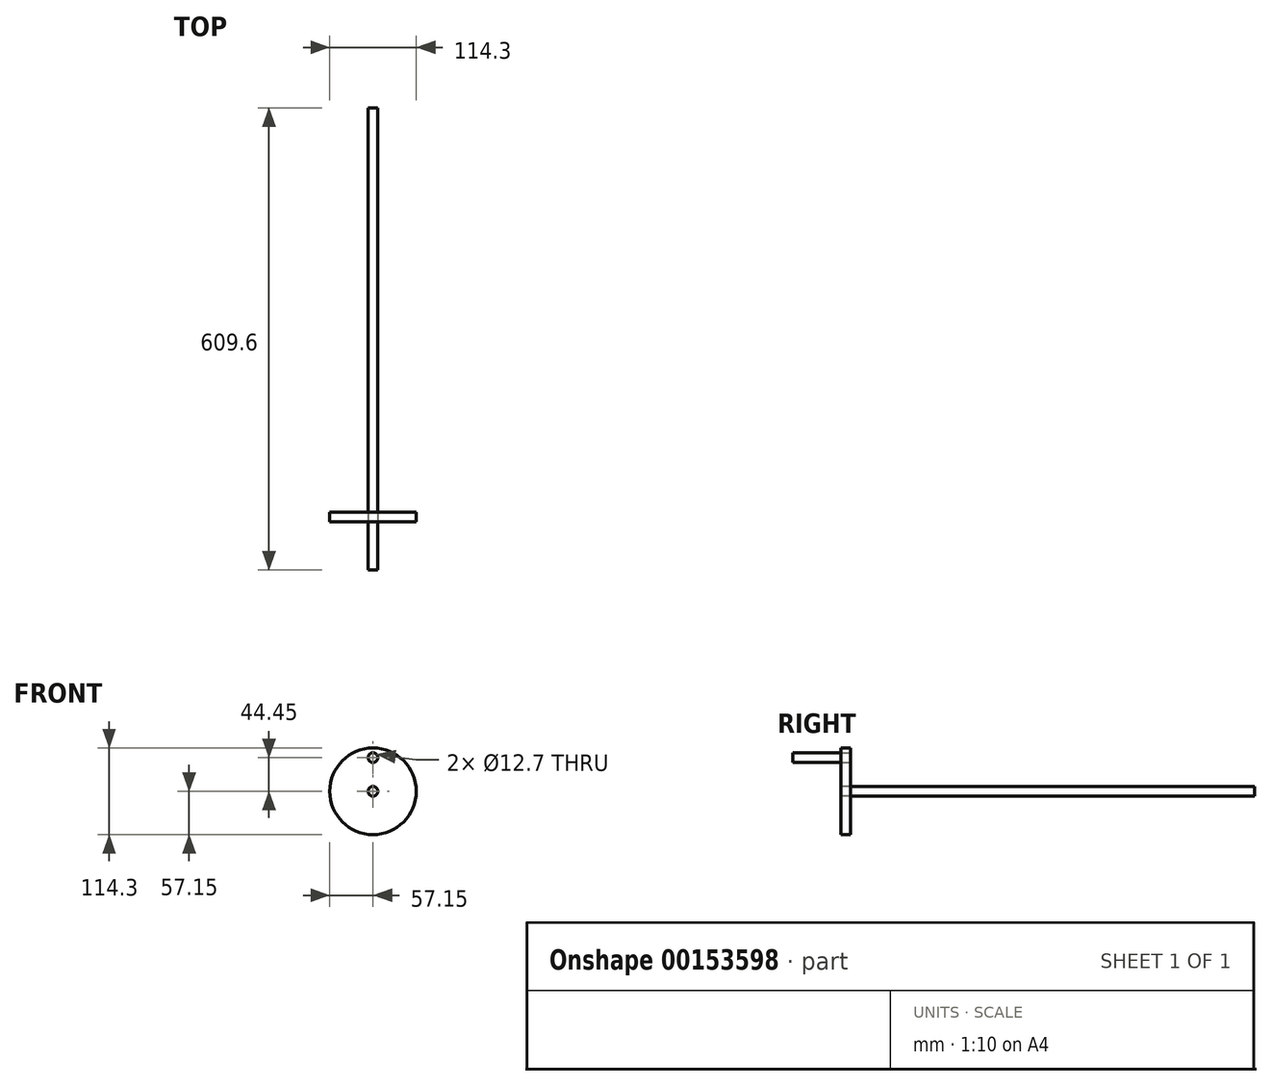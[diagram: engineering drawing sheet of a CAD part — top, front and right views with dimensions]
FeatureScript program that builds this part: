
annotation { "Feature Type Name" : "Feature", "Feature Type Description" : "" }
export const myFeature = defineFeature(function(context is Context, id is Id, definition is map)
    precondition{}
    {
        {
            var Q0;
            Q0=qCreatedBy(makeId("Front.planeOp"),FACE);
            var sketch = newSketch(context, id + "F0", { "sketchPlane" : qUnion([Q0])});
            skCircle(sketch, "E0", {"center": v(0, 0) * mm, "radius": 57.15 * mm});
            skSolve(sketch);
        }
        {
            var Q0;
            Q0=qSketchRegion(id+"F0",true);
            extrude(context, id + "F1", {"entities" : qUnion([Q0]), "depth" : 12.7 * mm});
        }
        {
            var Q0;
            Q0=makeQuery(id+"F1.opExtrude","CAP_FACE",FACE,{"disambiguationData":[OSD([sQuery(id+"F0.wireOp",EDGE,"E0")])],"isStart":false});
            var sketch = newSketch(context, id + "F2", { "sketchPlane" : qUnion([Q0])});
            skCircle(sketch, "E1", {"center": v(0, 0) * mm, "radius": 6.35 * mm});
            skSolve(sketch);
        }
        {
            var Q0;
            Q0=qSketchRegion(id+"F2",true);
            extrude(context, id + "F3", {"entities" : qUnion([Q0]), "operationType" : NewBodyOperationType.REMOVE, "endBound" : BoundingType.THROUGH_ALL, "oppositeDirection" : true, "depth" : 25.4 * mm});
        }
        {
            var Q0;
            Q0=makeQuery(id+"F1.opExtrude","CAP_FACE",FACE,{"disambiguationData":[OSD([sQuery(id+"F0.wireOp",EDGE,"E0")])],"isStart":false});
            var sketch = newSketch(context, id + "F4", { "sketchPlane" : qUnion([Q0])});
            skCircle(sketch, "E2", {"center": v(0, 0) * mm, "radius": 6.35 * mm});
            skSolve(sketch);
        }
        {
            var Q0;
            Q0=qSketchRegion(id+"F4",true);
            var Q1;
            Q1=sQuery(id+"F4.wireOp",EDGE,"E2");
            extrude(context, id + "F5", {"entities" : qUnion([Q0]), "surfaceEntities" : qUnion([Q1]), "oppositeDirection" : true, "depth" : 546.1 * mm});
        }
        {
            var Q0;
            Q0=makeQuery(id+"F1.opExtrude","CAP_FACE",FACE,{"disambiguationData":[OSD([sQuery(id+"F0.wireOp",EDGE,"E0")])],"isStart":true});
            var sketch = newSketch(context, id + "F6", { "sketchPlane" : qUnion([Q0])});
            skCircle(sketch, "E3", {"center": v(0, 44.45) * mm, "radius": 6.35 * mm});
            skLineSegment(sketch, "E4", {"start": v(0, 0) * mm, "end": v(0, 44.45) * mm, "construction": true});
            skSolve(sketch);
        }
        {
            var Q0;
            Q0=qSketchRegion(id+"F6",true);
            extrude(context, id + "F7", {"entities" : qUnion([Q0]), "operationType" : NewBodyOperationType.REMOVE, "endBound" : BoundingType.THROUGH_ALL, "oppositeDirection" : true, "depth" : 25.4 * mm});
        }
        {
            var Q0;
            Q0=makeQuery(id+"F6.imprint","IMPRINT",FACE,{"disambiguationData":[TD([[makeQuery(id+"F6.imprint","IMPRINT",EDGE,{"derivedFrom":sQuery(id+"F6.wireOp",EDGE,"E3")}),1.0]])]});
            var Q1;
            Q1=sQuery(id+"F6.wireOp",EDGE,"E3");
            extrude(context, id + "F8", {"entities" : qUnion([Q0]), "surfaceEntities" : qUnion([Q1]), "oppositeDirection" : true, "depth" : 76.2 * mm});
        }
    });
